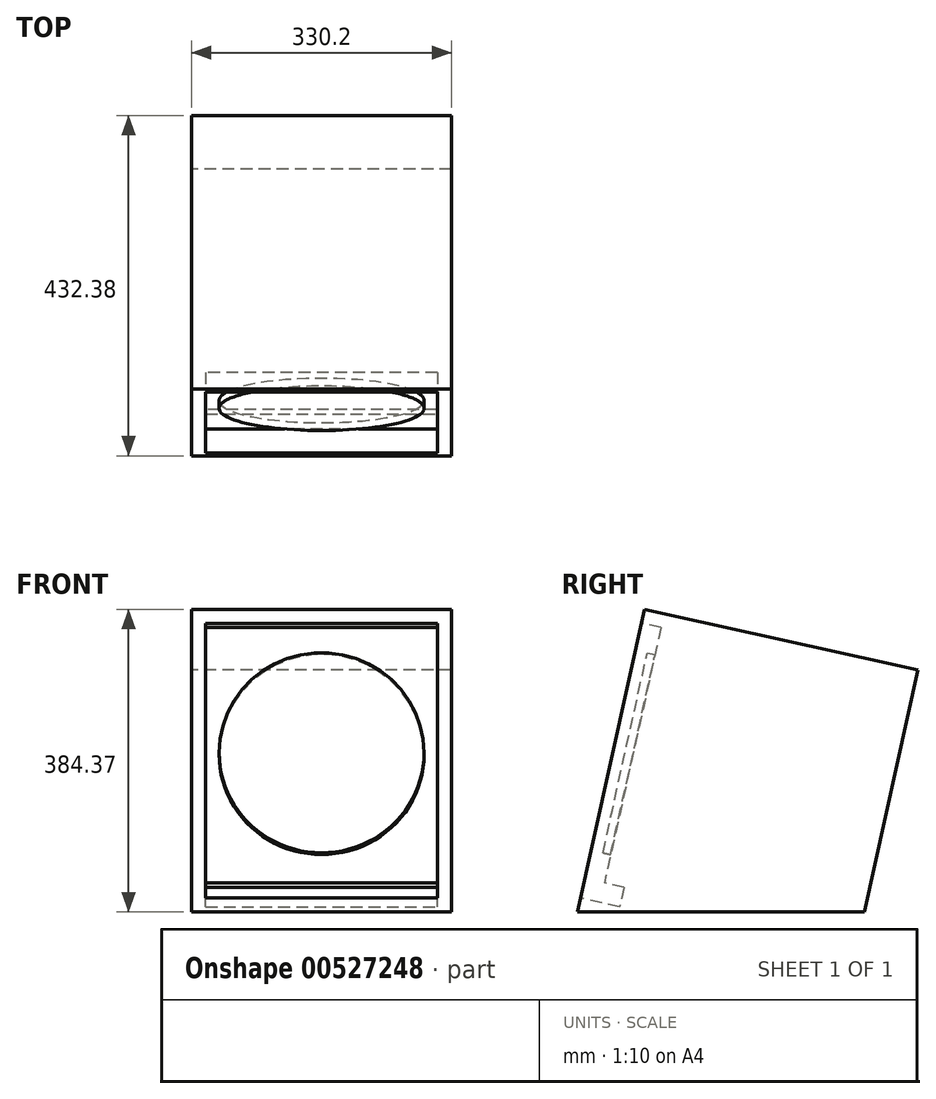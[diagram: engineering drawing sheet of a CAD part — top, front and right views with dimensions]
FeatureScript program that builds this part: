
annotation { "Feature Type Name" : "Feature", "Feature Type Description" : "" }
export const myFeature = defineFeature(function(context is Context, id is Id, definition is map)
    precondition{}
    {
        {
            var Q0;
            Q0=qCreatedBy(makeId("Right.planeOp"),FACE);
            var sketch = newSketch(context, id + "F0", { "sketchPlane" : qUnion([Q0])});
            skLineSegment(sketch, "E0", {"start": v(0, 0) * mm, "end": v(85.21, 384.37) * mm});
            skLineSegment(sketch, "E1", {"start": v(85.21, 384.37) * mm, "end": v(432.38, 307.4) * mm});
            skLineSegment(sketch, "E2", {"start": v(432.38, 307.4) * mm, "end": v(364.23, 0) * mm});
            skLineSegment(sketch, "E3", {"start": v(364.23, 0) * mm, "end": v(0, 0) * mm});
            skSolve(sketch);
        }
        {
            var Q0;
            Q0=makeQuery(id+"F0.imprint","IMPRINT",FACE,{"disambiguationData":[TD([[makeQuery(id+"F0.imprint","IMPRINT",EDGE,{"derivedFrom":sQuery(id+"F0.wireOp",EDGE,"E0")}),-1.0]])]});
            extrude(context, id + "F1", {"entities" : qUnion([Q0]), "depth" : 330.2 * mm, "offsetDistance" : 25.4 * mm});
        }
        {
            var Q0;
            Q0=makeQuery(id+"F1.opExtrude","SWEPT_FACE",FACE,{"disambiguationData":[OSD([sQuery(id+"F0.wireOp",EDGE,"E0")])]});
            var sketch = newSketch(context, id + "F2", { "sketchPlane" : qUnion([Q0])});
            skLineSegment(sketch, "E4", {"start": v(18.03, 375.67) * mm, "end": v(18.03, 18.03) * mm});
            skLineSegment(sketch, "E5", {"start": v(18.03, 18.03) * mm, "end": v(312.17, 18.03) * mm});
            skLineSegment(sketch, "E6", {"start": v(312.17, 18.03) * mm, "end": v(312.17, 375.67) * mm});
            skLineSegment(sketch, "E7", {"start": v(312.17, 375.67) * mm, "end": v(18.03, 375.67) * mm});
            skSolve(sketch);
        }
        {
            var Q0;
            Q0=makeQuery(id+"F2.imprint","IMPRINT",FACE,{"disambiguationData":[TD([[makeQuery(id+"F2.imprint","IMPRINT",EDGE,{"derivedFrom":sQuery(id+"F2.wireOp",EDGE,"E4")}),1.0]])]});
            extrude(context, id + "F3", {"entities" : qUnion([Q0]), "operationType" : NewBodyOperationType.REMOVE, "oppositeDirection" : true, "depth" : 25.4 * mm});
        }
        {
            var Q0;
            Q0=makeQuery(id+"F3.boolean.opBoolean","COPY",FACE,{"derivedFrom":makeQuery(id+"F3.opExtrude","CAP_FACE",FACE,{"disambiguationData":[OSD([sQuery(id+"F2.wireOp",EDGE,"E4"),sQuery(id+"F2.wireOp",EDGE,"E5"),sQuery(id+"F2.wireOp",EDGE,"E6"),sQuery(id+"F2.wireOp",EDGE,"E7")])],"isStart":false})});
            var sketch = newSketch(context, id + "F4", { "sketchPlane" : qUnion([Q0])});
            skCircle(sketch, "E8", {"center": v(165.1, 210.57) * mm, "radius": 130.18 * mm});
            skPoint(sketch, "E8.centerSnap0", {"position": v(165.1, 375.67) * mm});
            skSolve(sketch);
        }
        {
            var Q0;
            Q0=makeQuery(id+"F4.imprint","IMPRINT",FACE,{"disambiguationData":[TD([[makeQuery(id+"F4.imprint","IMPRINT",EDGE,{"derivedFrom":sQuery(id+"F4.wireOp",EDGE,"E8")}),1.0]])]});
            extrude(context, id + "F5", {"entities" : qUnion([Q0]), "operationType" : NewBodyOperationType.ADD, "depth" : 10.16 * mm});
        }
        {
            var Q0;
            Q0=makeQuery(id+"F3.boolean.opBoolean","COPY",FACE,{"derivedFrom":makeQuery(id+"F3.opExtrude","CAP_FACE",FACE,{"disambiguationData":[OSD([sQuery(id+"F2.wireOp",EDGE,"E4"),sQuery(id+"F2.wireOp",EDGE,"E5"),sQuery(id+"F2.wireOp",EDGE,"E6"),sQuery(id+"F2.wireOp",EDGE,"E7")])],"isStart":false})});
            var sketch = newSketch(context, id + "F6", { "sketchPlane" : qUnion([Q0])});
            skLineSegment(sketch, "E9", {"start": v(18.03, 18.03) * mm, "end": v(312.17, 18.03) * mm});
            skLineSegment(sketch, "E10", {"start": v(312.17, 18.03) * mm, "end": v(312.17, 43.43) * mm});
            skLineSegment(sketch, "E11", {"start": v(312.17, 43.43) * mm, "end": v(18.03, 43.43) * mm});
            skLineSegment(sketch, "E12", {"start": v(18.03, 43.43) * mm, "end": v(18.03, 18.03) * mm});
            skSolve(sketch);
        }
        {
            var Q0;
            Q0=makeQuery(id+"F6.imprint","IMPRINT",FACE,{"disambiguationData":[TD([[makeQuery(id+"F6.imprint","IMPRINT",EDGE,{"derivedFrom":sQuery(id+"F6.wireOp",EDGE,"E9")}),1.0]])]});
            extrude(context, id + "F7", {"entities" : qUnion([Q0]), "operationType" : NewBodyOperationType.REMOVE, "oppositeDirection" : true, "depth" : 25.4 * mm});
        }
    });
